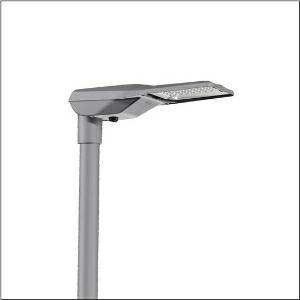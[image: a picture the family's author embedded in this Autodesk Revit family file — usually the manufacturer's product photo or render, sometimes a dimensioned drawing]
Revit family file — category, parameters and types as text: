
# Revit family: streetlight_sl_21_iq_mini___st1_0ab_5xe2m31u08hb_6af5
name_source: partatom
category: Lighting Fixtures
units: mm (PartAtom-declared; Revit-internal decimal feet)

## family parameters
Cut with Voids When Loaded = No
Host = Face
Light Source = No
Part Type = Normal
Room Calculation Point = No
Round Connector Dimension = Use Diameter
Shared = No

## types (1)
- --- (1 x LED, 8580 lm, 71 W, 3000K)
    Apparent Load = 71 VA
    CIE Flux Codes = 38 73 97 100 100
    Color Rendering = 70
    Color Temperature = 3000K
    Default Elevation = 1800 mm
    Description = Streetlight SL 21 iQ mini, mast luminaire, primary light control with lens, of PMMA, primary optical cover: cover, of toughened safety glass, transparent, light distribution: ST1.0aB, light emission: direct distribution, primary light characteristic: asymmetric, installation type: post-top, side-entry, LED, High Power LED, rated luminous flux: 8.580lm, luminous efficacy: 121lm/W, light colour: 730, colour temperature: 3000K, control gear: iQ-Street Remote, D4i with power reduction, control: pre-setting: logarithmic dimming characteristic, Street-Remote, Auto-Match, Temp-Guard, Lumen-Switch, Night-Set, Smart-Wire, Light-Fading, Desk-Remote (wireless, voltage-free reading and setting of iQ features in the workshop via application-optimized NFC function/RFID function), optimised constant luminous flux control (CLO 2.0), mains connection: 220..240V, AC, 50/60Hz, start of lifetime: 71W, end of service life: 75W, reduction: 30W, luminaire housing, of diecast aluminium, powder-coated, Siteco® metallic grey (DB 702S), corrosivity category C5 mid according to DIN EN ISO 12944, please order mast flange separately, inclination adjustable: 0°, 5°, 10°, 15°, sealing non-destructively replaceable, multi-level sealing system, length: 628mm, width: 235mm, height: 110mm, mast flange for spigot size: 42mm (side-entry): 5XC10008XM4, 60/48mm (side-entry/post-top): 5XC10108XM2, 76/60mm (side-entry/post-top): 5XC10108XM1, mounting height: 4..8m, Smart Interface below, protection rating (complete): IP66, insulation class (complete): insulation class II (safety insulation), certification: CE, ENEC, ENEC+, VDE, impact resistance: IK10, permissible operating ambient temperature for outdoor applications: -40..+50°C, standard-compliant lighting for roads and squares, packaging unit: 1 piece

Light Distribution: ST1.0aB
    Height = 110 mm
    Lamp = 1 x LED
    Lamp Light Flux = 8580 lm
    Lamp Power = 71 W
    Lamp count = 1
    Length = 625 mm
    Luminous efficacy = 121 lm/W
    Manufacturer = Siteco
    ModVariant = No
    Model = 5XE2M31U08HB
    Number of Poles = 1
    OnlyDefault = Yes
    Power Factor = 1
    Product Name = Streetlight SL 21 iQ mini | ST1.0aB
    Product group = mast luminaire | pylon top
    ProductGroupID = 6100
    Protection Class = Protection class II
    Protection Degree = IP 66
    RLX_Detail_Level = 1
    RLX_Emergency_Light_Flux = 0 lm
    RLX_Emergency_Type = 0
    RLX_Emergency_Type_DB = No
    RlxData = <blob elided: 92213 chars, md5=4371f2b9>
    Socket = socket
    Standby Power = 0 W
    System Light Flux = 8580 lm
    System Power = 71 W
    Type Comments = factory setting: luminous flux: 100 % | dim-lin: 254 | 716 mA
    Type Image = l_1003516.jpg
    URL = http://relux.com
    VarID = @adj_134033
    Voltage = 0 V
    Weight = 0.00 kg
    Width = 234 mm

## geometry (parser evidence)
native form markers: Blend x4, Sweep x11
no freeform markers — native parametric forms only
